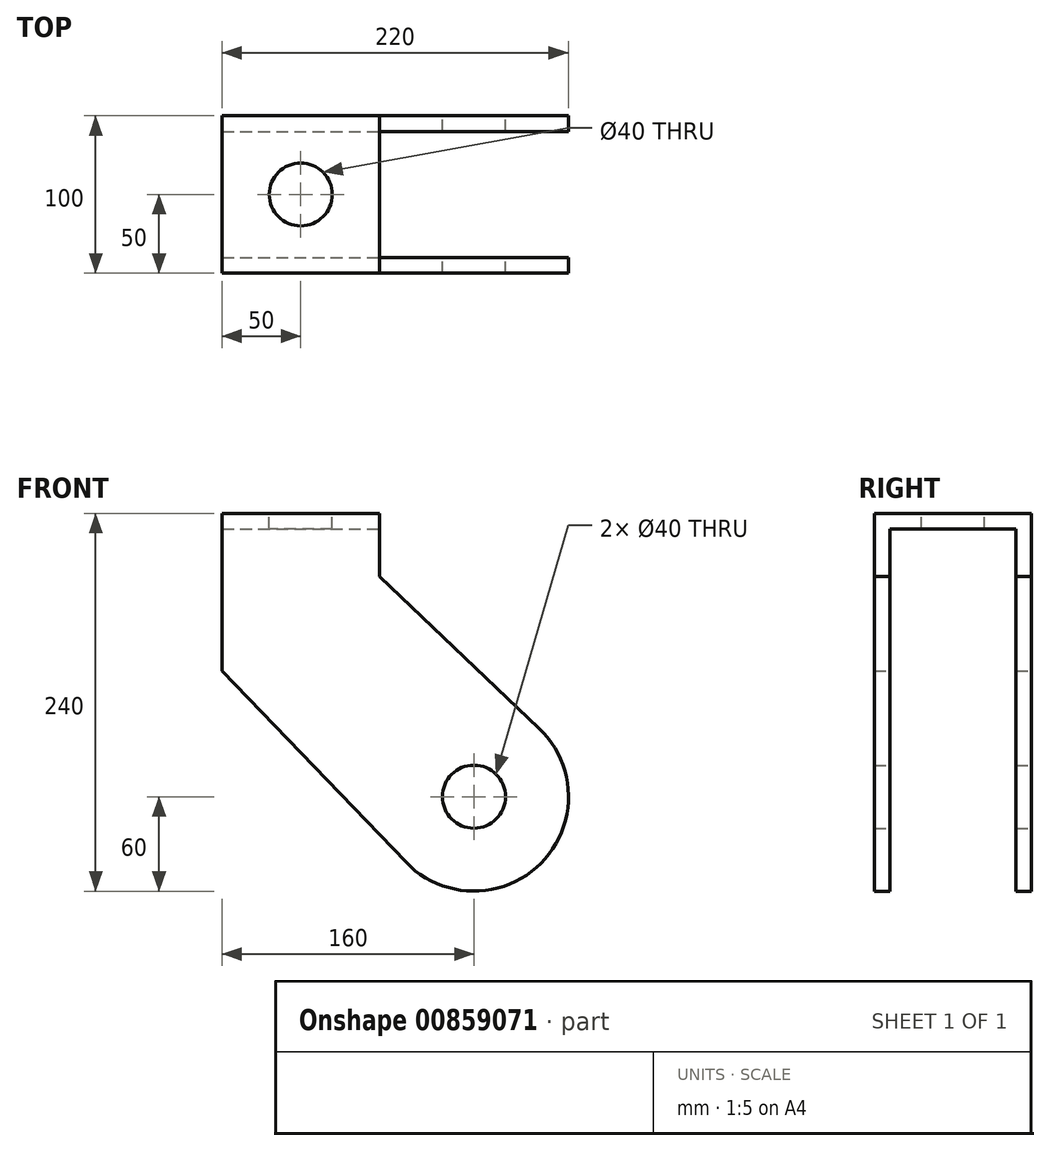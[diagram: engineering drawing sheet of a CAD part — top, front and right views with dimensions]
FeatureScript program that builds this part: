
annotation { "Feature Type Name" : "Feature", "Feature Type Description" : "" }
export const myFeature = defineFeature(function(context is Context, id is Id, definition is map)
    precondition{}
    {
        {
            var Q0;
            Q0=qCreatedBy(makeId("Front.planeOp"),FACE);
            var sketch = newSketch(context, id + "F0", { "sketchPlane" : qUnion([Q0])});
            skPoint(sketch, "E0.middle", {"position": v(0, 0) * mm});
            skLineSegment(sketch, "E1", {"start": v(-110, 120) * mm, "end": v(-10, 120) * mm});
            skLineSegment(sketch, "E2", {"start": v(-10, 120) * mm, "end": v(-10, 80) * mm});
            skLineSegment(sketch, "E3", {"start": v(-110, 120) * mm, "end": v(-110, 20) * mm});
            skCircle(sketch, "E4", {"center": v(50, -60) * mm, "radius": 20 * mm});
            skLineSegment(sketch, "E5", {"start": v(-10, 80) * mm, "end": v(91.38, -16.55) * mm});
            skLineSegment(sketch, "E6", {"start": v(-110, 20) * mm, "end": v(6.72, -101.56) * mm});
            skArc(sketch, "E7", {"start": v(91.38, -16.55) * mm, "mid": v(92.51, -102.34) * mm, "end": v(6.72, -101.56) * mm});
            skSolve(sketch);
        }
        {
            var Q0;
            Q0=makeQuery(id+"F0.imprint","IMPRINT",FACE,{"disambiguationData":[TD([[makeQuery(id+"F0.imprint","IMPRINT",EDGE,{"derivedFrom":sQuery(id+"F0.wireOp",EDGE,"E1")}),-1.0]])]});
            extrude(context, id + "F1", {"entities" : qUnion([Q0]), "depth" : 10 * mm, "offsetDistance" : 25 * mm});
        }
        {
            var Q0;
            Q0=makeQuery(id+"F1.opExtrude","CAP_FACE",FACE,{"disambiguationData":[OSD([sQuery(id+"F0.wireOp",EDGE,"E1"),sQuery(id+"F0.wireOp",EDGE,"E2"),sQuery(id+"F0.wireOp",EDGE,"E3"),sQuery(id+"F0.wireOp",EDGE,"E4"),sQuery(id+"F0.wireOp",EDGE,"E5"),sQuery(id+"F0.wireOp",EDGE,"E6"),sQuery(id+"F0.wireOp",EDGE,"E7")])],"isStart":false});
            var sketch = newSketch(context, id + "F2", { "sketchPlane" : qUnion([Q0])});
            skLineSegment(sketch, "E8", {"start": v(-110, 120) * mm, "end": v(-110, 110) * mm});
            skLineSegment(sketch, "E9", {"start": v(-110, 110) * mm, "end": v(-10, 110) * mm});
            skLineSegment(sketch, "E10", {"start": v(-10, 110) * mm, "end": v(-10, 120) * mm});
            skLineSegment(sketch, "E11", {"start": v(-10, 120) * mm, "end": v(-110, 120) * mm});
            skSolve(sketch);
        }
        {
            var Q0;
            Q0=makeQuery(id+"F2.imprint","IMPRINT",FACE,{"disambiguationData":[TD([[makeQuery(id+"F2.imprint","IMPRINT",EDGE,{"derivedFrom":sQuery(id+"F2.wireOp",EDGE,"E8")}),1.0]])]});
            extrude(context, id + "F3", {"entities" : qUnion([Q0]), "operationType" : NewBodyOperationType.ADD, "depth" : 80 * mm, "offsetDistance" : 25 * mm});
        }
        {
            var Q0;
            Q0=makeQuery(id+"F3.opExtrude","CAP_FACE",FACE,{"disambiguationData":[OSD([sQuery(id+"F2.wireOp",EDGE,"E8"),sQuery(id+"F2.wireOp",EDGE,"E9"),sQuery(id+"F2.wireOp",EDGE,"E10"),sQuery(id+"F2.wireOp",EDGE,"E11")])],"isStart":false});
            var sketch = newSketch(context, id + "F4", { "sketchPlane" : qUnion([Q0])});
            skLineSegment(sketch, "E12", {"start": v(-110, 120) * mm, "end": v(-110, 20) * mm});
            skLineSegment(sketch, "E13", {"start": v(-110, 120) * mm, "end": v(-10, 120) * mm});
            skLineSegment(sketch, "E14", {"start": v(-10, 120) * mm, "end": v(-10, 80) * mm});
            skCircle(sketch, "E15", {"center": v(50, -60) * mm, "radius": 20 * mm});
            skLineSegment(sketch, "E16", {"start": v(-10, 80) * mm, "end": v(91.38, -16.55) * mm});
            skLineSegment(sketch, "E17", {"start": v(-110, 20) * mm, "end": v(6.72, -101.56) * mm});
            skArc(sketch, "E18", {"start": v(91.38, -16.55) * mm, "mid": v(92.51, -102.34) * mm, "end": v(6.72, -101.56) * mm});
            skSolve(sketch);
        }
        {
            var Q0;
            Q0=makeQuery(id+"F4.imprint","IMPRINT",FACE,{"disambiguationData":[TD([[makeQuery(id+"F4.imprint","IMPRINT",EDGE,{"derivedFrom":sQuery(id+"F4.wireOp",EDGE,"E15")}),-1.0]])]});
            var Q1;
            {var subQ0=sQuery(id+"F4.wireOp",EDGE,"E13");Q1=makeQuery(id+"F4.imprint","IMPRINT",FACE,{"disambiguationData":[TD([[makeQuery(id+"F4.imprint","IMPRINT",EDGE,{"derivedFrom":subQ0}),-1.0]])]});}
            extrude(context, id + "F5", {"entities" : qUnion([Q0, Q1]), "operationType" : NewBodyOperationType.ADD, "depth" : 10 * mm, "offsetDistance" : 25 * mm});
        }
        {
            var Q0;
            Q0=makeQuery(id+"F5.boolean.opBoolean","MERGE",FACE,{"derivedFrom":[makeQuery(id+"F3.boolean.opBoolean","MERGE",FACE,{"derivedFrom":[makeQuery(id+"F1.opExtrude","SWEPT_FACE",FACE,{"disambiguationData":[OSD([sQuery(id+"F0.wireOp",EDGE,"E1")])]}),makeQuery(id+"F3.opExtrude","SWEPT_FACE",FACE,{"disambiguationData":[OSD([sQuery(id+"F2.wireOp",EDGE,"E11")])]})]}),makeQuery(id+"F5.opExtrude","SWEPT_FACE",FACE,{"disambiguationData":[OSD([sQuery(id+"F4.wireOp",EDGE,"E13")])]})]});
            var sketch = newSketch(context, id + "F6", { "sketchPlane" : qUnion([Q0])});
            skCircle(sketch, "E19", {"center": v(-60, -50) * mm, "radius": 20 * mm});
            skSolve(sketch);
        }
        {
            var Q0;
            Q0=makeQuery(id+"F6.imprint","IMPRINT",FACE,{"disambiguationData":[TD([[makeQuery(id+"F6.imprint","IMPRINT",EDGE,{"derivedFrom":sQuery(id+"F6.wireOp",EDGE,"E19")}),1.0]])]});
            extrude(context, id + "F7", {"entities" : qUnion([Q0]), "operationType" : NewBodyOperationType.REMOVE, "oppositeDirection" : true, "depth" : 25 * mm, "offsetDistance" : 25 * mm});
        }
    });
